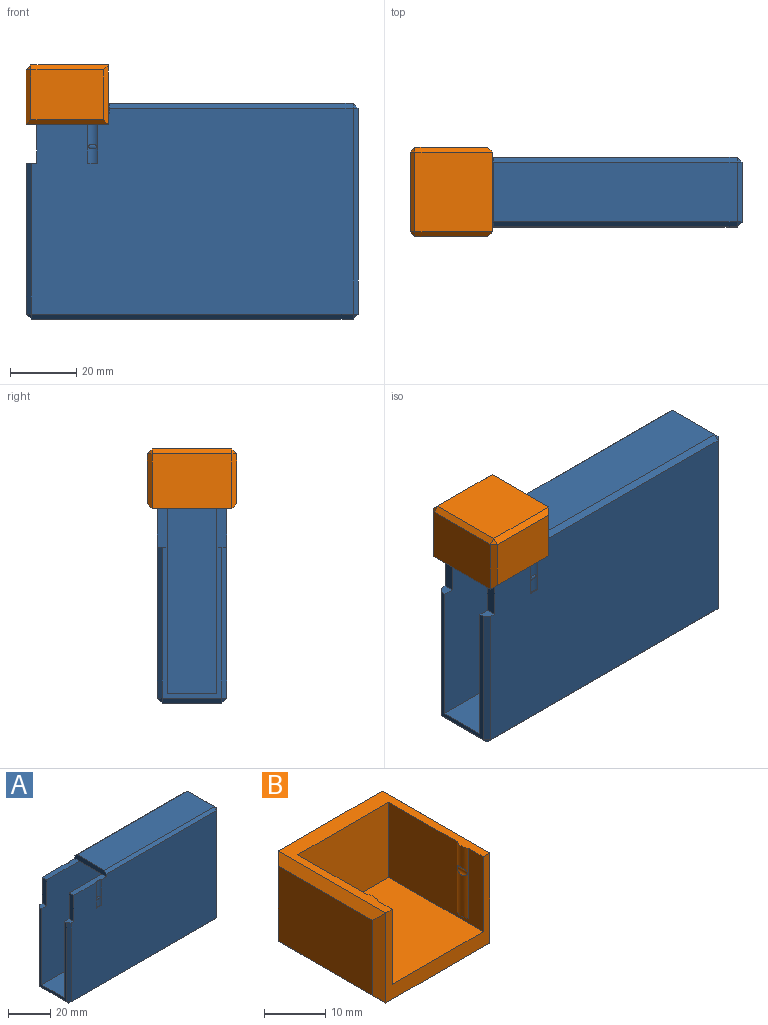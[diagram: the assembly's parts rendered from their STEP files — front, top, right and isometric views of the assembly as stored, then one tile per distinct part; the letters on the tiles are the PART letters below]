
ASSEMBLY  parts=2 mates=1
PART A: 41 faces, bbox 100x21x65 mm
  f0: cylinder r=2.5mm len=15mm, axis (0,0,1), area 45.4mm2, adj f6,f9,f15,f23
  f1: plane 45.5x18mm, normal (-1,0,0), area 159mm2, adj f2,f3,f12,f19,f21,f31,f37,f40
  f2: plane 90x59mm, normal (0,1,0), area 5262mm2, adj f1,f5,f7,f12,f13,f20,f21
  f3: plane 90x59mm, normal (0,-1,0), area 5262mm2, adj f1,f6,f7,f12,f13,f18,f19
  f4: plane 97x62mm, normal (0,-1,0), area 5908.3mm2, adj f5,f14,f16,f17,f20,f21,f24,f26
  f5: plane 21.8x3mm, normal (0,0,1), area 64.4mm2, adj f2,f4,f14,f16,f20
  f6: plane 21.8x3mm, normal (0,0,1), area 64.4mm2, adj f0,f3,f9,f14,f18
  f7: plane 65x15mm, normal (0,0,-1), area 975mm2, adj f2,f3,f13,f14
  f8: plane 62x18mm, normal (1,0,0), area 1116mm2, adj f26,f27,f33,f34
  f9: plane 97x62mm, normal (0,1,0), area 5908.3mm2, adj f0,f6,f14,f15,f18,f19,f28,f34
  f10: plane 73.5x18mm, normal (0,0,1), area 1323mm2, adj f14,f24,f27,f28
  f11: plane 97x18mm, normal (0,0,-1), area 1746mm2, adj f32,f33,f37,f38
  f12: plane 90x15mm, normal (0,0,1), area 1350mm2, adj f1,f2,f3,f13
  f13: plane 59x15mm, normal (-1,0,0), area 885mm2, adj f2,f3,f7,f12
  f14: plane 21x3mm, normal (-1,0,0), area 60.7mm2, adj f4,f5,f6,f7,f9,f10,f24,f28
  f15: plane 3x0.5mm, normal (0,0,1), area 1mm2, adj f0,f9
  f16: cylinder r=2.5mm len=15mm, axis (0,0,1), area 45.4mm2, adj f4,f5,f17,f22
  f17: plane 3x0.5mm, normal (0,0,1), area 1mm2, adj f4,f16
  f18: plane 15x3mm, normal (-1,0,0), area 45mm2, adj f3,f6,f9,f19
  f19: plane 3.2x3mm, normal (0,0,1), area 8.5mm2, adj f1,f3,f9,f18,f40
  f20: plane 15x3mm, normal (-1,0,0), area 45mm2, adj f2,f4,f5,f21
  f21: plane 3.2x3mm, normal (0,0,1), area 8.5mm2, adj f1,f2,f4,f20,f31
  f22: cylinder r=1mm len=2.38mm, axis (-1,0,0), area 3mm2, adj f16
  f23: cylinder r=1mm len=2.38mm, axis (-1,0,0), area 3mm2, adj f0
  f24: plane 73.5x1.5mm, normal (0,-0.71,0.71), area 155.9mm2, adj f4,f10,f14,f25
  f25: plane 1.5x1.5mm, normal (0.58,-0.58,0.58), area 1.9mm2, adj f24,f26,f27
  f26: plane 62x1.5mm, normal (0.71,-0.71,0), area 131.5mm2, adj f4,f8,f25,f29
  f27: plane 18x1.5mm, normal (0.71,0,0.71), area 38.2mm2, adj f8,f10,f25,f30
  f28: plane 73.5x1.5mm, normal (0,0.71,0.71), area 155.9mm2, adj f9,f10,f14,f30
  f29: plane 1.5x1.5mm, normal (0.58,-0.58,-0.58), area 1.9mm2, adj f26,f32,f33
  f30: plane 1.5x1.5mm, normal (0.58,0.58,0.58), area 1.9mm2, adj f27,f28,f34
  f31: plane 45.5x1.5mm, normal (-0.71,-0.71,0), area 96.5mm2, adj f1,f4,f21,f35
  f32: plane 97x1.5mm, normal (0,-0.71,-0.71), area 205.8mm2, adj f4,f11,f29,f35
  f33: plane 18x1.5mm, normal (0.71,0,-0.71), area 38.2mm2, adj f8,f11,f29,f36
  f34: plane 62x1.5mm, normal (0.71,0.71,0), area 131.5mm2, adj f8,f9,f30,f36
  f35: plane 1.5x1.5mm, normal (-0.58,-0.58,-0.58), area 1.9mm2, adj f31,f32,f37
  f36: plane 1.5x1.5mm, normal (0.58,0.58,-0.58), area 1.9mm2, adj f33,f34,f38
  f37: plane 18x1.5mm, normal (-0.71,0,-0.71), area 38.2mm2, adj f1,f11,f35,f39
  f38: plane 97x1.5mm, normal (0,0.71,-0.71), area 205.8mm2, adj f9,f11,f36,f39
  f39: plane 1.5x1.5mm, normal (-0.58,0.58,-0.58), area 1.9mm2, adj f37,f38,f40
  f40: plane 45.5x1.5mm, normal (-0.71,0.71,0), area 96.5mm2, adj f1,f9,f19,f39
PART B: 27 faces, bbox 27x24.8x18 mm
  f0: cylinder r=2.4mm len=14mm, axis (0,0,1), area 36.4mm2, adj f6,f9,f13,f14
  f1: plane 21.8x15mm, normal (1,0,0), area 289.9mm2, adj f2,f6,f8,f10,f11,f12
  f2: plane 24x18mm, normal (0,-1,0), area 117mm2, adj f1,f6,f7,f9,f10,f17,f21
  f3: plane 21.8x15mm, normal (1,0,0), area 327mm2, adj f21,f23,f24,f26
  f4: plane 24x16.5mm, normal (0,1,0), area 396mm2, adj f6,f18,f22,f26
  f5: plane 21.8x15mm, normal (-1,0,0), area 327mm2, adj f16,f17,f18,f19
  f6: plane 24.8x24mm, normal (0,0,1), area 138.8mm2, adj f0,f1,f2,f4,f8,f9,f11,f16
  f7: plane 24x23.3mm, normal (0,0,-1), area 559.2mm2, adj f2,f19,f22,f23
  f8: plane 21x15mm, normal (0,-1,0), area 315mm2, adj f1,f6,f9,f10
  f9: plane 21.8x15mm, normal (-1,0,0), area 289.9mm2, adj f0,f2,f6,f8,f10,f13
  f10: plane 21.8x21mm, normal (0,0,1), area 457.8mm2, adj f1,f2,f8,f9
  f11: cylinder r=2.4mm len=14mm, axis (0,0,1), area 36.4mm2, adj f1,f6,f12,f15
  f12: plane 2.65x0.4mm, normal (0,0,-1), area 0.7mm2, adj f1,f11
  f13: plane 2.65x0.4mm, normal (0,0,-1), area 0.7mm2, adj f0,f9
  f14: cylinder r=1.1mm len=2.32mm, axis (0,-1,0), area 3mm2, adj f0
  f15: cylinder r=1.1mm len=2.32mm, axis (0,-1,0), area 3mm2, adj f11
  f16: plane 24.8x1.5mm, normal (-0.71,0,0.71), area 49.4mm2, adj f5,f6,f17,f18
  f17: plane 18x1.5mm, normal (-0.71,-0.71,0), area 35mm2, adj f2,f5,f16,f19
  f18: plane 16.5x1.5mm, normal (-0.71,0.71,0), area 33.4mm2, adj f4,f5,f16,f20
  f19: plane 23.3x1.5mm, normal (-0.71,0,-0.71), area 47.8mm2, adj f5,f7,f17,f20
  f20: plane 1.5x1.5mm, normal (-0.58,0.58,-0.58), area 1.9mm2, adj f18,f19,f22
  f21: plane 18x1.5mm, normal (0.71,-0.71,0), area 35mm2, adj f2,f3,f23,f24
  f22: plane 24x1.5mm, normal (0,0.71,-0.71), area 50.9mm2, adj f4,f7,f20,f25
  f23: plane 23.3x1.5mm, normal (0.71,0,-0.71), area 47.8mm2, adj f3,f7,f21,f25
  f24: plane 24.8x1.5mm, normal (0.71,0,0.71), area 49.4mm2, adj f3,f6,f21,f26
  f25: plane 1.5x1.5mm, normal (0.58,0.58,-0.58), area 1.9mm2, adj f22,f23,f26
  f26: plane 16.5x1.5mm, normal (0.71,0.71,0), area 33.4mm2, adj f3,f4,f24,f25
PLACE A t=(-15.01,18.63,-16.77)mm
PLACE B rot(axis=(0.71,-0.71,0),180deg) t=(-52.71,18.63,59.86)mm
MATE cylindrical B.f11 <-> A.f0  axis (0,0,-1) through (-45.01,31.13,48.86)mm
